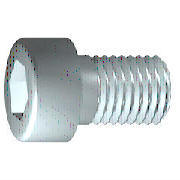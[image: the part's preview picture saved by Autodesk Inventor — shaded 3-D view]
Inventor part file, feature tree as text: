
AUTODESK INVENTOR PART (.ipt)
format: ipt  version: 2022 (Build 260153000, 153)  size: 200,192 bytes
history: native  units: mm (DEFAULTED — no unit token found)
features: sketch x2, other x1, extrude x1, plane x1, fillet x1
ambient origin geometry x7: Origin, YZ Plane, XY Plane, X Axis, Y Axis, Z Axis, Center Point
bodies: Solid1 (feature_tree)
feature tree (6):
  other  "Cuerpo"
  extrude  "Ranura"  Depth=4.0mm
  plane  "Work Plane1"
  fillet  "Fillet2"  Radius=4.0mm
  sketch  "Boceto1"  dims[d1=4.25mm d2=0.429515mm d3=4.0mm]
  sketch  "Boceto2"  dims[d4=2.0mm d5=60.0deg d6=4.0mm d7=4.0mm d8=3.464102mm d9=7.0mm d10=90.0deg d11=10.0mm d12=0.0mm d13=4.25mm d14=0.0mm d15=0.429415mm d16=0.429415mm d17=0.4mm d19=0.0mm d26=6.0mm d27=45.0deg d28=0.0mm d29=0.0mm d30=0.1mm]
